# Revit family: Bird_Spikes_Nixalite_H
name_source: partatom
category: Specialty Equipment
revit_build: Autodesk Revit 2015 (Build: 20140223_1515(x64)
units: mm (PartAtom-declared; Revit-internal decimal feet)

## types (1)
- Model H
    Assembly Code = E1090900
    Base = Metal - Stainless Steel
    Construction Details = http://www.arcat.com
    Default Elevation = 0' - 0"
    Description = Nixalite Bird Spike System - Premium Model H as Specified
    Expected Lifespan (Years) = 0
    Green Building-LEED = http://www.arcat.com
    Installation_Fabricaton = http://www.nixalite.com
    Keynote = 10290
    Maintenance Schedule (Months) = 0
    Manufacturer = Nixalite Architectural Bird Control
    Manufacturer Fax = 888-624-1196
    Manufacturer Website = http://www.nixalite.com
    Model = Premium Model H
    Product Data = http://www.arcat.com
    Sales Information = http://www.nixalite.com
    Send Message = http://www.arcat.com
    Specification = http://arcat.com
    URL = http://www.nixalite.com
    Warranty Duration (Years) = 0
    Wire Finish = Metal - Stainless Steel
    Wire Points per Foot = 60
    Wire Spacing = 0' - 0 3/16"
    Wires Points per Bundle = 5
    halfspace = 0' - 0 3/32"

## geometry (parser evidence)
native form markers: Blend x2, Sweep x5
no freeform markers — native parametric forms only
